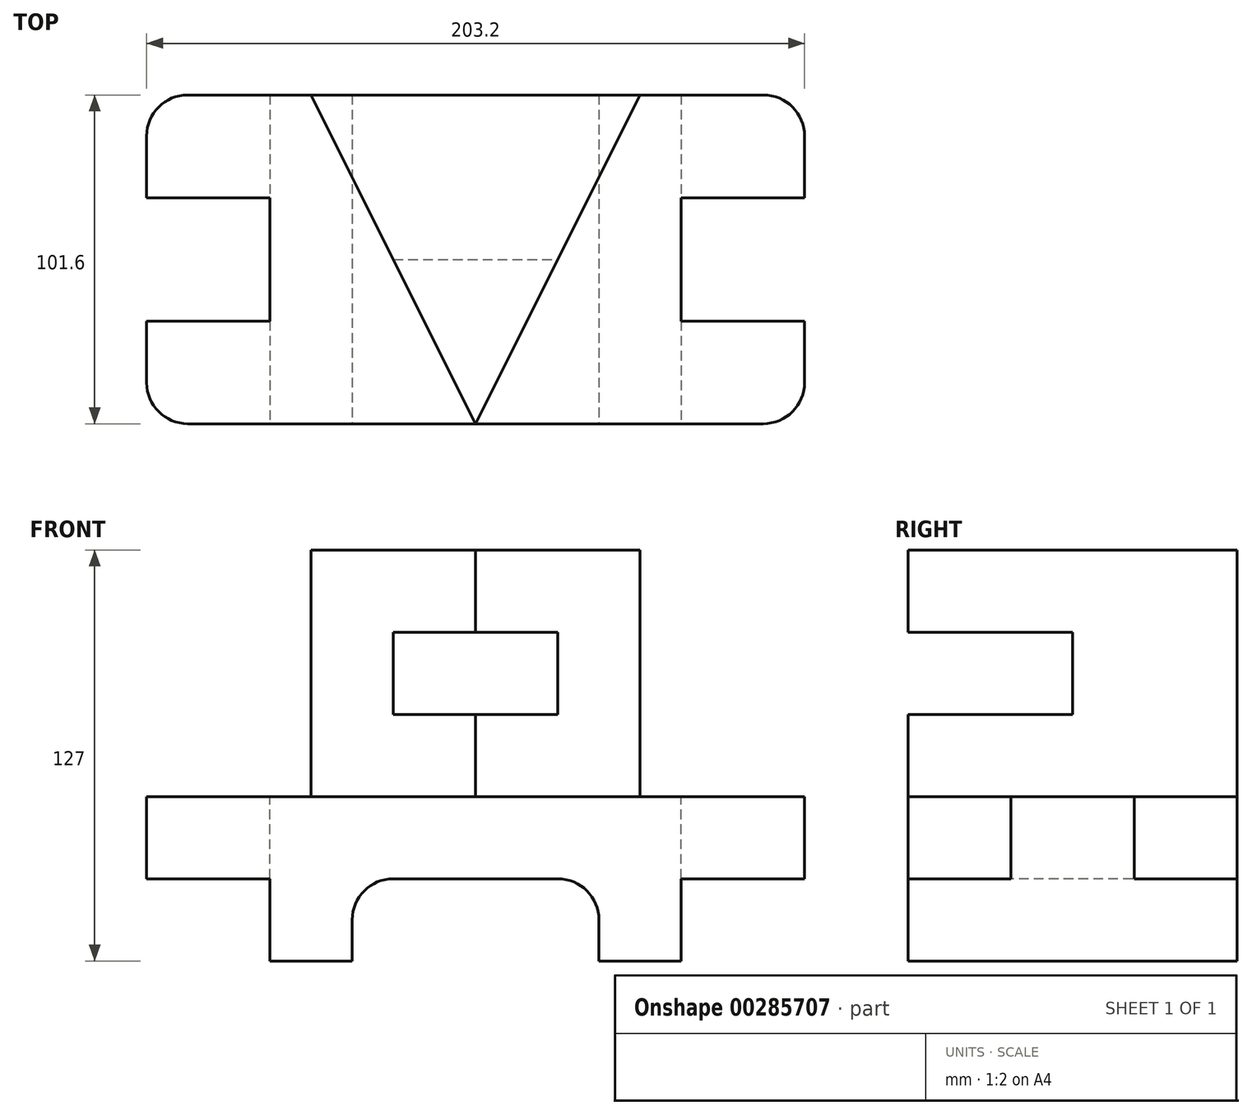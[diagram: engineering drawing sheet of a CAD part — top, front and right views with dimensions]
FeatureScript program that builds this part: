
annotation { "Feature Type Name" : "Feature", "Feature Type Description" : "" }
export const myFeature = defineFeature(function(context is Context, id is Id, definition is map)
    precondition{}
    {
        {
            var Q0;
            Q0=qCreatedBy(makeId("Front.planeOp"),FACE);
            var sketch = newSketch(context, id + "F0", { "sketchPlane" : qUnion([Q0])});
            skLineSegment(sketch, "E0.bottom", {"start": v(0, 0) * mm, "end": v(25.4, 0) * mm});
            skLineSegment(sketch, "E0.top", {"start": v(0, 25.4) * mm, "end": v(25.4, 25.4) * mm});
            skLineSegment(sketch, "E0.left", {"start": v(0, 0) * mm, "end": v(0, 25.4) * mm});
            skLineSegment(sketch, "E0.right", {"start": v(25.4, 0) * mm, "end": v(25.4, 25.4) * mm});
            skLineSegment(sketch, "E1", {"start": v(0, 25.4) * mm, "end": v(-38.1, 25.4) * mm});
            skLineSegment(sketch, "E2", {"start": v(-38.1, 25.4) * mm, "end": v(-38.1, 50.8) * mm});
            skLineSegment(sketch, "E3", {"start": v(-38.1, 50.8) * mm, "end": v(165.1, 50.8) * mm});
            skLineSegment(sketch, "E4", {"start": v(165.1, 50.8) * mm, "end": v(165.1, 25.4) * mm});
            skLineSegment(sketch, "E5", {"start": v(165.1, 25.4) * mm, "end": v(127, 25.4) * mm});
            skLineSegment(sketch, "E6.bottom", {"start": v(127, 25.4) * mm, "end": v(101.6, 25.4) * mm});
            skLineSegment(sketch, "E6.top", {"start": v(127, 0) * mm, "end": v(101.6, 0) * mm});
            skLineSegment(sketch, "E6.left", {"start": v(127, 25.4) * mm, "end": v(127, 0) * mm});
            skLineSegment(sketch, "E6.right", {"start": v(101.6, 25.4) * mm, "end": v(101.6, 0) * mm});
            skLineSegment(sketch, "E7", {"start": v(25.4, 25.4) * mm, "end": v(101.6, 25.4) * mm});
            skLineSegment(sketch, "E8.bottom", {"start": v(25.4, 25.4) * mm, "end": v(38.1, 25.4) * mm});
            skLineSegment(sketch, "E8.left", {"start": v(25.4, 25.4) * mm, "end": v(25.4, 12.7) * mm});
            skLineSegment(sketch, "E9.bottom", {"start": v(101.6, 25.4) * mm, "end": v(88.9, 25.4) * mm});
            skLineSegment(sketch, "E9.left", {"start": v(101.6, 25.4) * mm, "end": v(101.6, 12.7) * mm});
            skArc(sketch, "E10", {"start": v(38.1, 25.4) * mm, "mid": v(29.12, 21.68) * mm, "end": v(25.4, 12.7) * mm});
            skArc(sketch, "E11", {"start": v(101.6, 12.7) * mm, "mid": v(97.88, 21.68) * mm, "end": v(88.9, 25.4) * mm});
            skSolve(sketch);
        }
        {
            var Q0;
            Q0 = qSketchRegion(id + "F0", true);
            extrude(context, id + "F1", {"entities" : qUnion([Q0]), "endBound" : BoundingType.SYMMETRIC, "oppositeDirection" : true, "depth" : 101.6 * mm});
        }
        {
            var Q0;
            Q0=makeQuery(id+"F1.opExtrude","SWEPT_FACE",FACE,{"disambiguationData":[OSD([sQuery(id+"F0.wireOp",EDGE,"E3")])]});
            var sketch = newSketch(context, id + "F2", { "sketchPlane" : qUnion([Q0])});
            skLineSegment(sketch, "E12", {"start": v(-38.1, -50.8) * mm, "end": v(-38.1, -19.05) * mm});
            skLineSegment(sketch, "E13", {"start": v(-38.1, -19.05) * mm, "end": v(0, -19.05) * mm});
            skLineSegment(sketch, "E14", {"start": v(-38.1, 50.8) * mm, "end": v(-38.1, 19.05) * mm});
            skLineSegment(sketch, "E15", {"start": v(-38.1, 19.05) * mm, "end": v(0, 19.05) * mm});
            skLineSegment(sketch, "E16", {"start": v(0, 19.05) * mm, "end": v(0, -19.05) * mm});
            skLineSegment(sketch, "E17", {"start": v(-38.1, 19.05) * mm, "end": v(-38.1, -19.05) * mm});
            skLineSegment(sketch, "E18", {"start": v(-38.1, 19.05) * mm, "end": v(-38.1, 38.1) * mm});
            skLineSegment(sketch, "E19", {"start": v(-38.1, -19.05) * mm, "end": v(-38.1, -34.93) * mm});
            skLineSegment(sketch, "E20", {"start": v(-38.1, -19.05) * mm, "end": v(-38.1, -38.1) * mm});
            skLineSegment(sketch, "E21", {"start": v(-38.1, 50.8) * mm, "end": v(-25.4, 50.8) * mm});
            skLineSegment(sketch, "E22", {"start": v(-38.1, -50.8) * mm, "end": v(-25.4, -50.8) * mm});
            skLineSegment(sketch, "E23", {"start": v(165.1, 50.8) * mm, "end": v(152.4, 50.8) * mm});
            skLineSegment(sketch, "E24", {"start": v(165.1, 50.8) * mm, "end": v(165.1, 19.05) * mm});
            skLineSegment(sketch, "E25", {"start": v(165.1, 19.05) * mm, "end": v(127, 19.05) * mm});
            skLineSegment(sketch, "E26", {"start": v(127, 19.05) * mm, "end": v(127, -19.05) * mm});
            skLineSegment(sketch, "E27", {"start": v(127, -19.05) * mm, "end": v(165.1, -19.05) * mm});
            skLineSegment(sketch, "E28", {"start": v(165.1, -19.05) * mm, "end": v(165.1, -50.8) * mm});
            skLineSegment(sketch, "E29", {"start": v(165.1, -50.8) * mm, "end": v(152.4, -50.8) * mm});
            skLineSegment(sketch, "E30", {"start": v(165.1, -19.05) * mm, "end": v(165.1, -38.1) * mm});
            skLineSegment(sketch, "E31", {"start": v(165.1, 19.05) * mm, "end": v(165.1, 38.1) * mm});
            skLineSegment(sketch, "E32", {"start": v(165.1, 19.05) * mm, "end": v(165.1, -19.05) * mm});
            skArc(sketch, "E33", {"start": v(-25.4, 50.8) * mm, "mid": v(-34.38, 47.08) * mm, "end": v(-38.1, 38.1) * mm});
            skArc(sketch, "E34", {"start": v(-38.1, -38.1) * mm, "mid": v(-34.38, -47.08) * mm, "end": v(-25.4, -50.8) * mm});
            skLineSegment(sketch, "E35", {"start": v(114.3, 50.8) * mm, "end": v(12.7, 50.8) * mm});
            skLineSegment(sketch, "E36", {"start": v(12.7, 50.8) * mm, "end": v(63.5, -50.8) * mm});
            skLineSegment(sketch, "E37", {"start": v(63.5, -50.8) * mm, "end": v(114.3, 50.8) * mm});
            skLineSegment(sketch, "E38", {"start": v(114.3, 50.8) * mm, "end": v(165.1, 50.8) * mm});
            skLineSegment(sketch, "E39", {"start": v(12.7, 50.8) * mm, "end": v(-38.1, 50.8) * mm});
            skArc(sketch, "E40", {"start": v(165.1, 38.1) * mm, "mid": v(161.38, 47.08) * mm, "end": v(152.4, 50.8) * mm});
            skArc(sketch, "E41", {"start": v(152.4, -50.8) * mm, "mid": v(161.38, -47.08) * mm, "end": v(165.1, -38.1) * mm});
            skSolve(sketch);
        }
        {
            var Q0;
            {var subQ0=sQuery(id+"F2.wireOp",EDGE,"E14");Q0=makeQuery(id+"F2.imprint","IMPRINT",FACE,{"disambiguationData":[TD([[makeQuery(id+"F2.imprint","IMPRINT",EDGE,{"derivedFrom":subQ0}),1.0]])]});}
            var Q1;
            Q1=makeQuery(id+"F2.imprint","IMPRINT",FACE,{"disambiguationData":[TD([[makeQuery(id+"F2.imprint","IMPRINT",EDGE,{"derivedFrom":sQuery(id+"F2.wireOp",EDGE,"E12")}),1.0]])]});
            var Q2;
            Q2=makeQuery(id+"F2.imprint","IMPRINT",FACE,{"disambiguationData":[TD([[makeQuery(id+"F2.imprint","IMPRINT",EDGE,{"derivedFrom":sQuery(id+"F2.wireOp",EDGE,"E13")}),1.0]])]});
            var Q3;
            Q3=makeQuery(id+"F2.imprint","IMPRINT",FACE,{"disambiguationData":[TD([[makeQuery(id+"F2.imprint","IMPRINT",EDGE,{"derivedFrom":sQuery(id+"F2.wireOp",EDGE,"E25")}),1.0]])]});
            var Q4;
            {var subQ0=sQuery(id+"F2.wireOp",EDGE,"E24");Q4=makeQuery(id+"F2.imprint","IMPRINT",FACE,{"disambiguationData":[TD([[makeQuery(id+"F2.imprint","IMPRINT",EDGE,{"derivedFrom":subQ0}),-1.0]])]});}
            var Q5;
            Q5=makeQuery(id+"F2.imprint","IMPRINT",FACE,{"disambiguationData":[TD([[makeQuery(id+"F2.imprint","IMPRINT",EDGE,{"derivedFrom":sQuery(id+"F2.wireOp",EDGE,"E28")}),-1.0]])]});
            extrude(context, id + "F3", {"entities" : qUnion([Q0, Q1, Q2, Q3, Q4, Q5]), "operationType" : NewBodyOperationType.REMOVE, "oppositeDirection" : true, "depth" : 25.4 * mm});
        }
        {
            var Q0;
            Q0=makeQuery(id+"F2.imprint","IMPRINT",FACE,{"disambiguationData":[TD([[makeQuery(id+"F2.imprint","IMPRINT",EDGE,{"derivedFrom":sQuery(id+"F2.wireOp",EDGE,"E35")}),-1.0]])]});
            extrude(context, id + "F4", {"entities" : qUnion([Q0]), "operationType" : NewBodyOperationType.ADD, "depth" : 25.4 * mm});
        }
        {
            var Q0;
            Q0=makeQuery(id+"F4.opExtrude","CAP_FACE",FACE,{"disambiguationData":[OSD([sQuery(id+"F2.wireOp",EDGE,"E35"),sQuery(id+"F2.wireOp",EDGE,"E36"),sQuery(id+"F2.wireOp",EDGE,"E37")])],"isStart":false});
            var sketch = newSketch(context, id + "F5", { "sketchPlane" : qUnion([Q0])});
            skLineSegment(sketch, "E42", {"start": v(38.1, 0) * mm, "end": v(88.9, 0) * mm});
            skSolve(sketch);
        }
        {
            var Q0;
            {var subQ0=sQuery(id+"F5.wireOp",EDGE,"E42");Q0=makeQuery(id+"F5.imprint","IMPRINT",FACE,{"disambiguationData":[TD([[makeQuery(id+"F5.imprint","IMPRINT",EDGE,{"derivedFrom":subQ0}),1.0]])]});}
            extrude(context, id + "F6", {"entities" : qUnion([Q0]), "operationType" : NewBodyOperationType.ADD, "depth" : 25.4 * mm});
        }
        {
            var Q0;
            Q0=makeQuery(id+"F6.opExtrude","CAP_FACE",FACE,{"disambiguationData":[OSD([sQuery(id+"F2.wireOp",EDGE,"E35"),sQuery(id+"F2.wireOp",EDGE,"E36"),sQuery(id+"F2.wireOp",EDGE,"E37"),sQuery(id+"F5.wireOp",EDGE,"E42")])],"isStart":false});
            var sketch = newSketch(context, id + "F7", { "sketchPlane" : qUnion([Q0])});
            skLineSegment(sketch, "E43", {"start": v(12.7, 50.8) * mm, "end": v(63.5, -50.8) * mm});
            skLineSegment(sketch, "E44", {"start": v(63.5, -50.8) * mm, "end": v(114.3, 50.8) * mm});
            skLineSegment(sketch, "E45", {"start": v(114.3, 50.8) * mm, "end": v(12.7, 50.8) * mm});
            skSolve(sketch);
        }
        {
            var Q0;
            Q0 = qSketchRegion(id + "F7", true);
            extrude(context, id + "F8", {"entities" : qUnion([Q0]), "operationType" : NewBodyOperationType.ADD, "depth" : 25.4 * mm});
        }
    });
